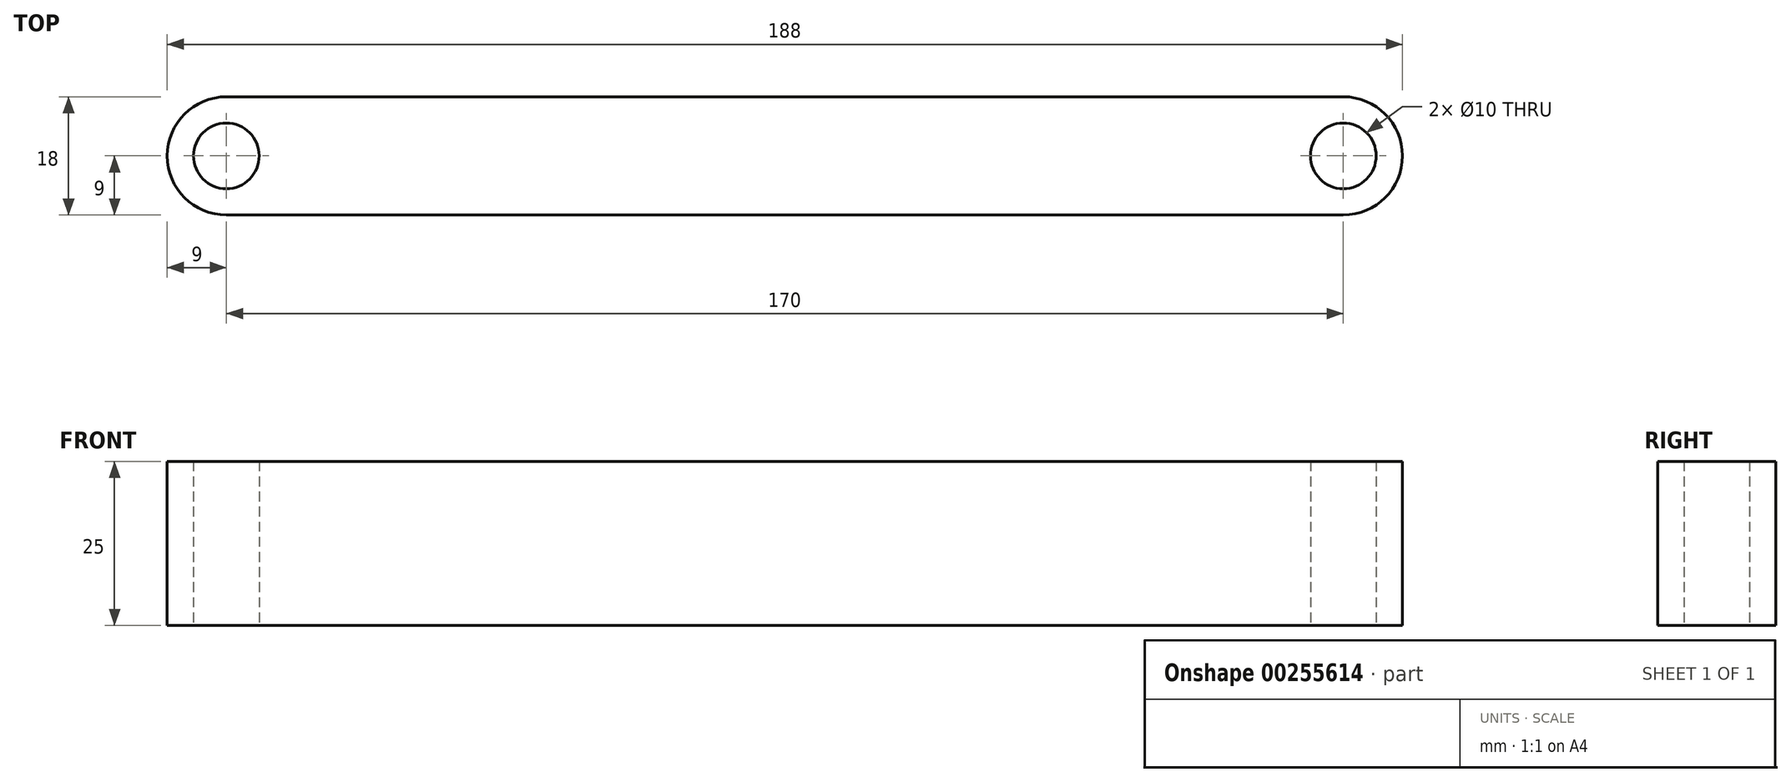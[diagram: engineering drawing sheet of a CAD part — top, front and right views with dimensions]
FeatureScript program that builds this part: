
annotation { "Feature Type Name" : "Feature", "Feature Type Description" : "" }
export const myFeature = defineFeature(function(context is Context, id is Id, definition is map)
    precondition{}
    {
        {
            var Q0;
            Q0=qCreatedBy(makeId("Top.planeOp"),FACE);
            var sketch = newSketch(context, id + "F0", { "sketchPlane" : qUnion([Q0])});
            skCircle(sketch, "E0", {"center": v(0, 0) * mm, "radius": 5 * mm});
            skCircle(sketch, "E1", {"center": v(170, 0) * mm, "radius": 5 * mm});
            skArc(sketch, "E2", {"start": v(0, 9) * mm, "mid": v(-9, 0) * mm, "end": v(0, -9) * mm});
            skArc(sketch, "E3", {"start": v(170, -9) * mm, "mid": v(179, 0) * mm, "end": v(170, 9) * mm});
            skLineSegment(sketch, "E4", {"start": v(0, 9) * mm, "end": v(170, 9) * mm});
            skLineSegment(sketch, "E5", {"start": v(0, -9) * mm, "end": v(170, -9) * mm});
            skSolve(sketch);
        }
        {
            var Q0;
            Q0=makeQuery(id+"F0.imprint","IMPRINT",FACE,{"disambiguationData":[TD([[makeQuery(id+"F0.imprint","IMPRINT",EDGE,{"derivedFrom":sQuery(id+"F0.wireOp",EDGE,"E0")}),-1.0]])]});
            extrude(context, id + "F1", {"entities" : qUnion([Q0]), "depth" : 25 * mm});
        }
    });
